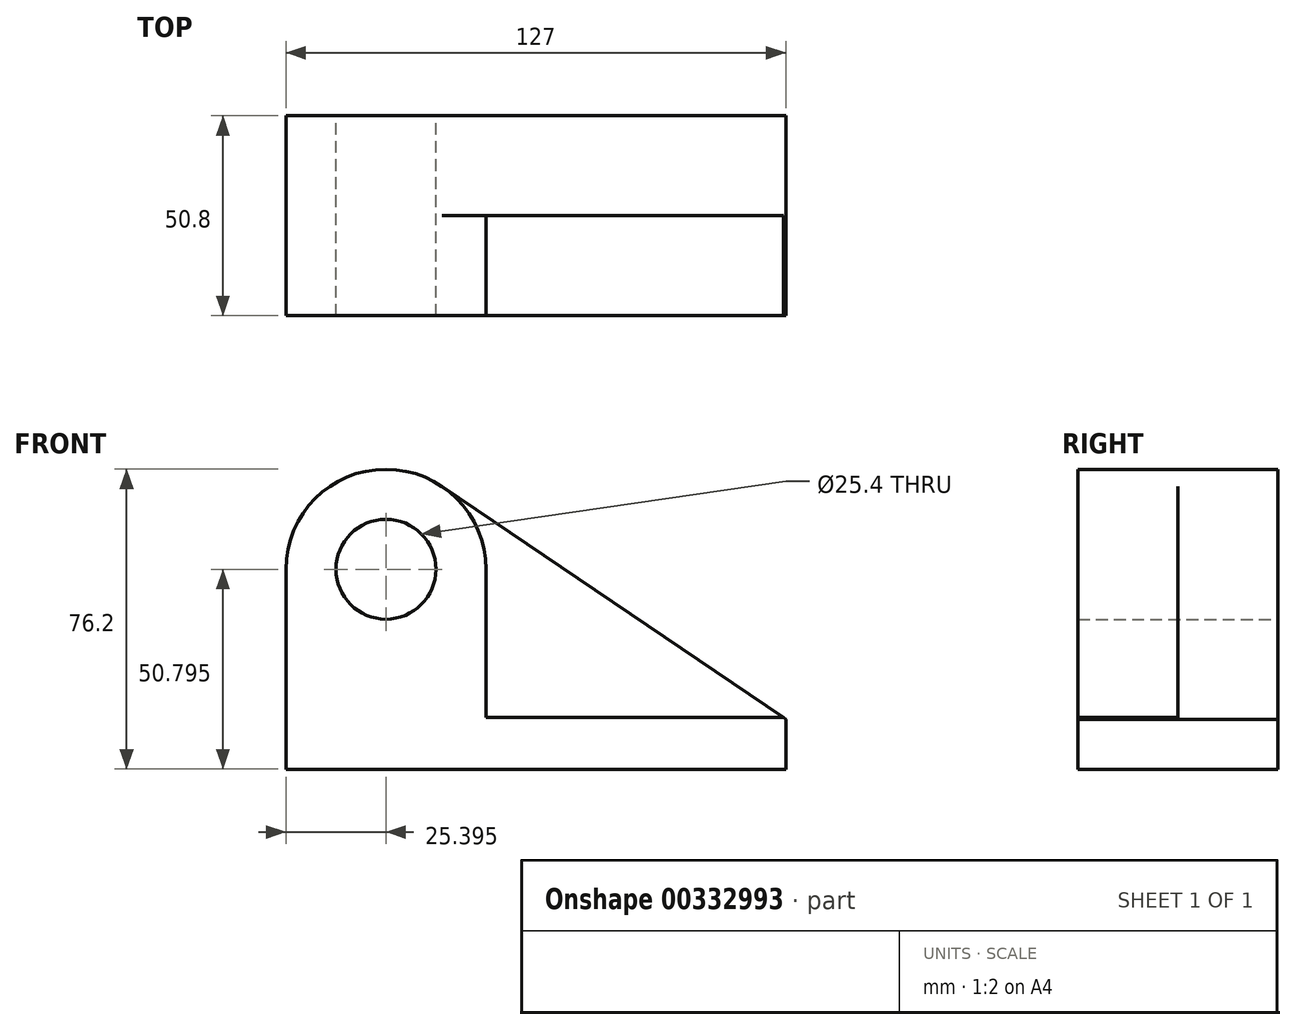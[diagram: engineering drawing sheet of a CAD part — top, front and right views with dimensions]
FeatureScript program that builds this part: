
annotation { "Feature Type Name" : "Feature", "Feature Type Description" : "" }
export const myFeature = defineFeature(function(context is Context, id is Id, definition is map)
    precondition{}
    {
        {
            var Q0;
            Q0=qCreatedBy(makeId("Front.planeOp"),FACE);
            var sketch = newSketch(context, id + "F0", { "sketchPlane" : qUnion([Q0])});
            skCircle(sketch, "E0", {"center": v(-29.95, 37.66) * mm, "radius": 12.7 * mm});
            skArc(sketch, "E1", {"start": v(-15.72, 58.69) * mm, "mid": v(-41.86, 60.1) * mm, "end": v(-55.35, 37.66) * mm});
            skLineSegment(sketch, "E2", {"start": v(-55.35, 37.66) * mm, "end": v(-55.35, -13.14) * mm});
            skLineSegment(sketch, "E3", {"start": v(-55.35, -13.14) * mm, "end": v(71.65, -13.14) * mm});
            skLineSegment(sketch, "E4", {"start": v(71.65, -13.14) * mm, "end": v(71.65, -0.44) * mm});
            skLineSegment(sketch, "E5", {"start": v(71.65, -0.44) * mm, "end": v(-15.72, 58.69) * mm});
            skSolve(sketch);
        }
        {
            var Q0;
            Q0=makeQuery(id+"F0.imprint","IMPRINT",FACE,{"disambiguationData":[TD([[makeQuery(id+"F0.imprint","IMPRINT",EDGE,{"derivedFrom":sQuery(id+"F0.wireOp",EDGE,"E0")}),-1.0]])]});
            extrude(context, id + "F1", {"entities" : qUnion([Q0]), "depth" : 25.4 * mm});
        }
        {
            var Q0;
            Q0=makeQuery(id+"F1.opExtrude","CAP_FACE",FACE,{"disambiguationData":[OSD([sQuery(id+"F0.wireOp",EDGE,"E0"),sQuery(id+"F0.wireOp",EDGE,"E1"),sQuery(id+"F0.wireOp",EDGE,"E2"),sQuery(id+"F0.wireOp",EDGE,"E3"),sQuery(id+"F0.wireOp",EDGE,"E4"),sQuery(id+"F0.wireOp",EDGE,"E5")])],"isStart":false});
            var sketch = newSketch(context, id + "F2", { "sketchPlane" : qUnion([Q0])});
            skCircle(sketch, "E6", {"center": v(-29.95, 37.66) * mm, "radius": 12.7 * mm});
            skArc(sketch, "E7", {"start": v(-4.55, 37.66) * mm, "mid": v(-29.95, 63.06) * mm, "end": v(-55.35, 37.66) * mm});
            skLineSegment(sketch, "E8.bottom", {"start": v(71.65, -13.14) * mm, "end": v(-55.35, -13.14) * mm});
            skLineSegment(sketch, "E8.top", {"start": v(71.65, 0) * mm, "end": v(-4.55, 0) * mm});
            skLineSegment(sketch, "E8.left", {"start": v(71.65, -13.14) * mm, "end": v(71.65, 0) * mm});
            skLineSegment(sketch, "E8.right", {"start": v(-55.35, -13.14) * mm, "end": v(-55.35, 0) * mm});
            skLineSegment(sketch, "E9", {"start": v(-4.55, 37.66) * mm, "end": v(-4.55, 0) * mm});
            skSolve(sketch);
        }
        {
            var Q0;
            Q0=makeQuery(id+"F2.imprint","IMPRINT",FACE,{"disambiguationData":[TD([[makeQuery(id+"F2.imprint","IMPRINT",EDGE,{"derivedFrom":sQuery(id+"F2.wireOp",EDGE,"E6")}),-1.0]])]});
            extrude(context, id + "F3", {"entities" : qUnion([Q0]), "operationType" : NewBodyOperationType.ADD, "depth" : 25.4 * mm});
        }
    });
